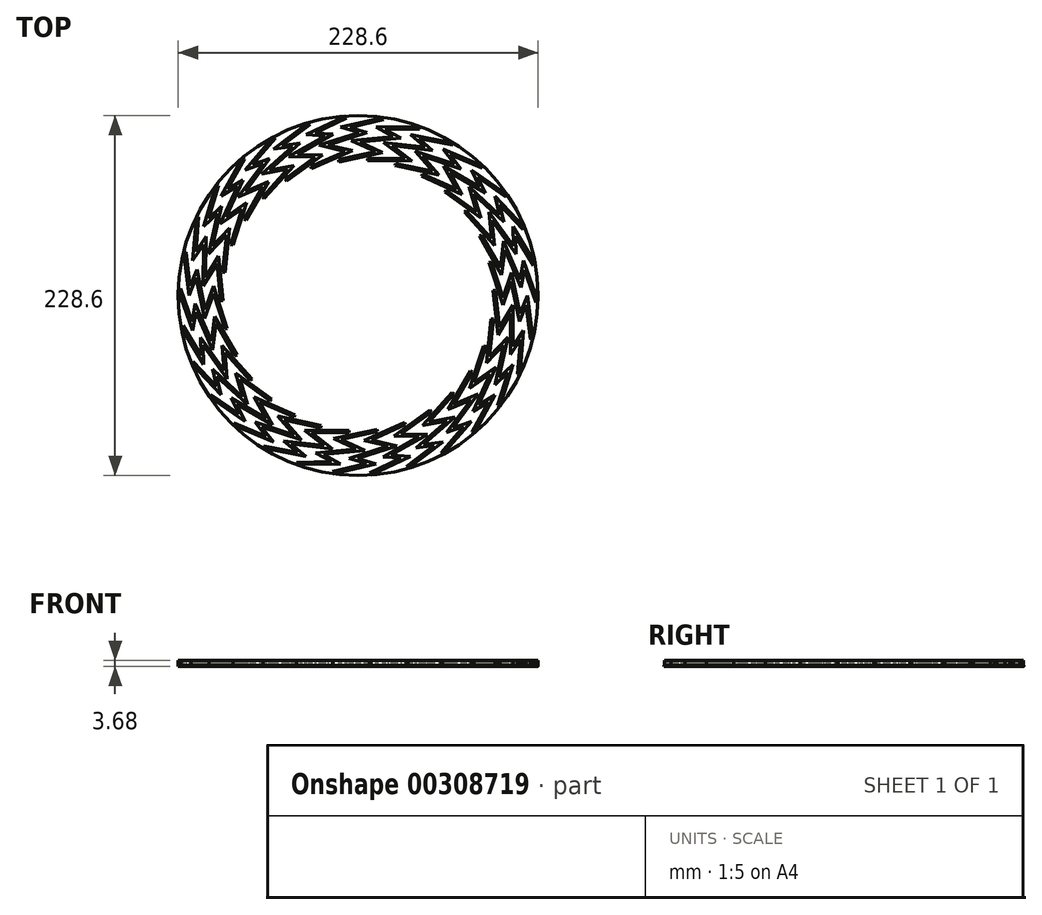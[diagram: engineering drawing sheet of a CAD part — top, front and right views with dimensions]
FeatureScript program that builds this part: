
annotation { "Feature Type Name" : "Feature", "Feature Type Description" : "" }
export const myFeature = defineFeature(function(context is Context, id is Id, definition is map)
    precondition{}
    {
        {
            var Q0;
            Q0=qCreatedBy(makeId("Top.planeOp"),FACE);
            var sketch = newSketch(context, id + "F0", { "sketchPlane" : qUnion([Q0])});
            skCircle(sketch, "E0", {"center": v(0, 0) * mm, "radius": 114.3 * mm});
            skCircle(sketch, "E1", {"center": v(0, 0) * mm, "radius": 87.31 * mm, "construction": true});
            skSolve(sketch);
        }
        {
            var Q0;
            Q0 = qSketchRegion(id + "F0", true);
            extrude(context, id + "F1", {"entities" : qUnion([Q0]), "depth" : 0.5 * mm});
        }
        {
            var Q0;
            Q0=makeQuery(id+"F1.opExtrude","CAP_FACE",FACE,{"disambiguationData":[OSD([sQuery(id+"F0.wireOp",EDGE,"E0")])],"isStart":false});
            var sketch = newSketch(context, id + "F2", { "sketchPlane" : qUnion([Q0])});
            skCircle(sketch, "E2", {"center": v(0, 0) * mm, "radius": 87.31 * mm, "construction": true});
            skLineSegment(sketch, "E3", {"start": v(-110.92, 27.6) * mm, "end": v(-107.47, 0) * mm});
            skLineSegment(sketch, "E4", {"start": v(-107.47, 0) * mm, "end": v(-102.82, 11.3) * mm});
            skLineSegment(sketch, "E5", {"start": v(-102.82, 11.3) * mm, "end": v(-97.54, -14.69) * mm});
            skLineSegment(sketch, "E6", {"start": v(-97.54, -14.69) * mm, "end": v(-92, 1.27) * mm});
            skLineSegment(sketch, "E7", {"start": v(-92, 1.27) * mm, "end": v(-84.66, -21.36) * mm});
            skLineSegment(sketch, "E8.0", {"start": v(-91.94, 6.05) * mm, "end": v(-83.2, -20.9) * mm});
            skLineSegment(sketch, "E8.1", {"start": v(-109.4, 27.79) * mm, "end": v(-106.68, 5.94) * mm});
            skLineSegment(sketch, "E8.2", {"start": v(-106.68, 5.94) * mm, "end": v(-102.33, 16.52) * mm});
            skLineSegment(sketch, "E8.3", {"start": v(-102.33, 16.52) * mm, "end": v(-97.15, -8.94) * mm});
            skLineSegment(sketch, "E8.4", {"start": v(-97.15, -8.94) * mm, "end": v(-91.94, 6.05) * mm});
            skLineSegment(sketch, "E9", {"start": v(-110.92, 27.6) * mm, "end": v(-109.4, 27.79) * mm});
            skLineSegment(sketch, "E10", {"start": v(-83.2, -20.9) * mm, "end": v(-84.66, -21.36) * mm});
            skSolve(sketch);
        }
        {
            var Q0;
            Q0 = qSketchRegion(id + "F2", true);
            extrude(context, id + "F3", {"entities" : qUnion([Q0]), "operationType" : NewBodyOperationType.ADD, "depth" : 3.17 * mm});
        }
        {
            var Q0;
            Q0=makeQuery(id+"F1.opExtrude","SWEPT_BODY",BODY,{"disambiguationData":[OSD([sQuery(id+"F0.wireOp",EDGE,"E0")])]});
            var Q1;
            Q1=makeQuery(id+"F1.opExtrude","CAP_EDGE",EDGE,{"disambiguationData":[OSD([sQuery(id+"F0.wireOp",EDGE,"E0")])],"isStart":false});
            circularPattern(context, id + "F4", {"entities" : qUnion([Q0]), "axis" : qUnion([Q1]), "angle" : 360 * degree, "instanceCount" : 30, "equalSpace" : true});
        }
    });
